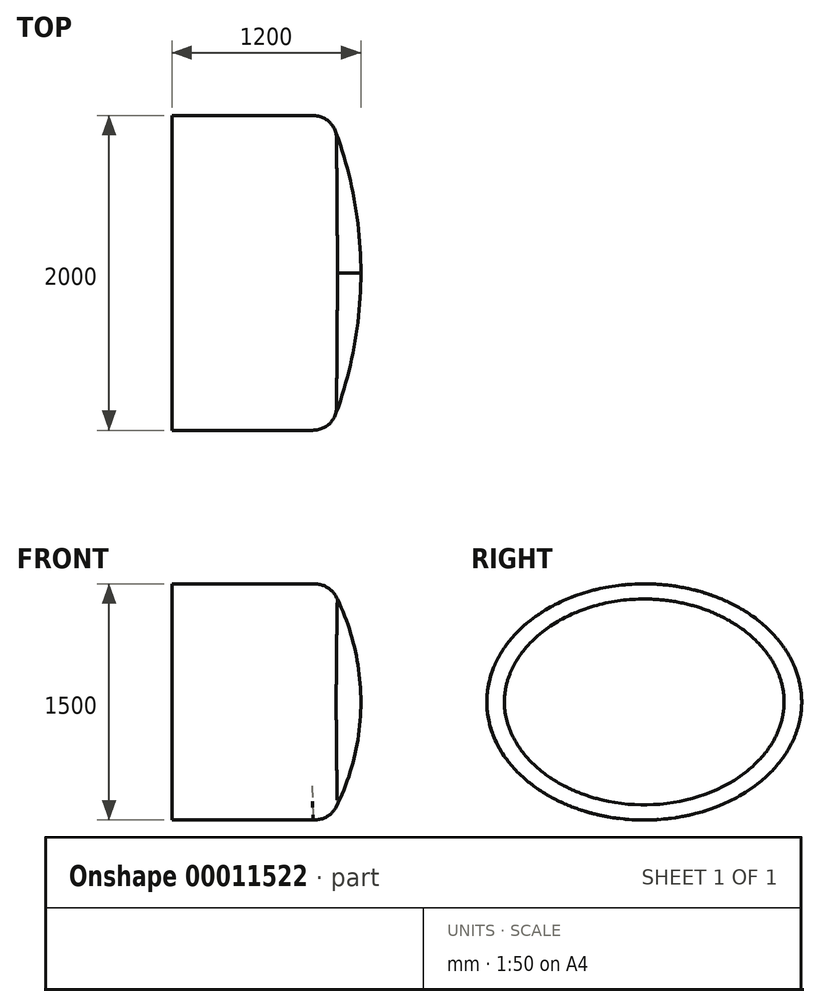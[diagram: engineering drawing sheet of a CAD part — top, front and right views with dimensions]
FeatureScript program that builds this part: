
annotation { "Feature Type Name" : "Feature", "Feature Type Description" : "" }
export const myFeature = defineFeature(function(context is Context, id is Id, definition is map)
    precondition{}
    {
        {
            var Q0;
            Q0=qCreatedBy(makeId("Right.planeOp"),FACE);
            var sketch = newSketch(context, id + "F0", { "sketchPlane" : qUnion([Q0])});
            skEllipse(sketch, "E0", {"center": v(0, 0) * mm, "majorRadius": 1000 * mm, "minorRadius": 750 * mm, "majorAxis": v(1, 0)});
            skSolve(sketch);
        }
        {
            var Q0;
            Q0=qCreatedBy(makeId("Front.planeOp"),FACE);
            var sketch = newSketch(context, id + "F1", { "sketchPlane" : qUnion([Q0])});
            skArc(sketch, "E1", {"start": v(0, -750) * mm, "mid": v(149.14, -388.1) * mm, "end": v(200, 0) * mm});
            skArc(sketch, "E2", {"start": v(200, 0) * mm, "mid": v(149.14, 388.1) * mm, "end": v(0, 750) * mm});
            skSolve(sketch);
        }
        {
            var Q0;
            Q0=qCreatedBy(makeId("Top.planeOp"),FACE);
            var sketch = newSketch(context, id + "F2", { "sketchPlane" : qUnion([Q0])});
            skArc(sketch, "E3", {"start": v(0, -1000) * mm, "mid": v(149.5, -509.9) * mm, "end": v(200, 0) * mm});
            skArc(sketch, "E4", {"start": v(200, 0) * mm, "mid": v(149.5, 509.9) * mm, "end": v(0, 1000) * mm});
            skSolve(sketch);
        }
        {
            var Q0;
            Q0=makeQuery(id+"F0.imprint","IMPRINT",FACE,{"disambiguationData":[TD([[makeQuery(id+"F0.imprint","IMPRINT",EDGE,{"derivedFrom":sQuery(id+"F0.wireOp",EDGE,"E0")}),1.0]])]});
            var Q1;
            Q1=sQuery(id+"F1.wireOp",VERTEX,"E1.end");
            var Q2;
            Q2=sQuery(id+"F0.wireOp",EDGE,"E0");
            var Q3;
            Q3=sQuery(id+"F1.wireOp",VERTEX,"E1.end");
            var Q4;
            Q4=sQuery(id+"F1.wireOp",EDGE,"E2");
            var Q5;
            Q5=sQuery(id+"F2.wireOp",EDGE,"E3");
            var Q6;
            Q6=sQuery(id+"F2.wireOp",EDGE,"E4");
            var Q7;
            Q7=sQuery(id+"F1.wireOp",EDGE,"E1");
            loft(context, id + "F3", {"bodyType" : ToolBodyType.SURFACE, "addGuides" : true, "sheetProfilesArray" : [{ "sheetProfileEntities" : qUnion([Q0]) }, { "sheetProfileEntities" : qUnion([Q1]) }], "wireProfilesArray" : [{ "wireProfileEntities" : qUnion([Q2]) }, { "wireProfileEntities" : qUnion([Q3]) }], "guidesArray" : [{ "guideEntities" : qUnion([Q4]), "guideDerivativeType" : LoftGuideDerivativeType.DEFAULT, "guideDerivativeMagnitude" : 1 }, { "guideEntities" : qUnion([Q5]), "guideDerivativeType" : LoftGuideDerivativeType.DEFAULT, "guideDerivativeMagnitude" : 1 }, { "guideEntities" : qUnion([Q6]), "guideDerivativeType" : LoftGuideDerivativeType.DEFAULT, "guideDerivativeMagnitude" : 1 }, { "guideEntities" : qUnion([Q7]), "guideDerivativeType" : LoftGuideDerivativeType.DEFAULT, "guideDerivativeMagnitude" : 1 }]});
        }
        {
            var Q0;
            Q0=qSketchRegion(id+"F0",true);
            var Q1;
            Q1=makeQuery(id+"F3.opLoft","SWEPT_FACE",FACE,{"disambiguationData":[OSD([sQuery(id+"F0.wireOp",EDGE,"E0"),sQuery(id+"F1.wireOp",VERTEX,"E2.end"),sQuery(id+"F1.wireOp",EDGE,"E2"),sQuery(id+"F2.wireOp",VERTEX,"E3.start"),sQuery(id+"F2.wireOp",EDGE,"E3")])]});
            extrude(context, id + "F4", {"entities" : qUnion([Q0]), "endBound" : BoundingType.UP_TO_SURFACE, "endBoundEntityFace" : qUnion([Q1]), "depth" : 25 * mm, "hasSecondDirection" : true, "secondDirectionOppositeDirection" : true, "secondDirectionDepth" : 1000 * mm});
        }
        {
            var Q0;
            Q0=makeQuery(id+"F4.opExtrude","CAP_EDGE",EDGE,{"disambiguationData":[OSD([sQuery(id+"F0.wireOp",EDGE,"E0")]),OD(6.0)],"isStart":false});
            fillet(context, id + "F5", {"entities" : qUnion([Q0]), "radius" : 170 * mm, "tangentPropagation" : true, "rho" : 0.5, "crossSection" : FilletCrossSection.CONIC, "allowEdgeOverflow" : false});
        }
    });
